# Revit family: OHMH-NRG
name_source: partatom
category: Mechanical Equipment
units: mm (PartAtom-declared; Revit-internal decimal feet)

## family parameters
Always vertical = Yes
Cut with Voids When Loaded = No
OmniClass Number = 23.40.40.11.17
OmniClass Title = Refrigerated Cases
Part Type = Normal
Room Calculation Point = No
Round Connector Dimension = Use Radius
Shared = No
Work Plane-Based = Yes

## types (12) — shared parameters
16" Shelf = Yes
18" Shelf = Yes
20" Shelf = Yes
BOTTOM ELECTRICAL = Yes
BOTTOM REFRIGERATION PIPING = Yes
Certifications = NSF 7, UL471, CSA
DATE = 05/16/2016
DESIGNERS NAME = SHIDDRAMESH
DRAIN PIPING = Yes
Default Elevation = 48"
Defrosts Per Day = 6
Description = High Multi-Deck Merchandiser
Discharge Air (°F) = 30 °F
Discharge Air Velocity (FPM) = 200 FPM
EQUIPMENT DESCRIPTION = High Multi-Deck Merchandiser
EQUIPMENT MARK = OHMH-NRG-5BF
Evaporator (°F) = 27 °F
GLASS = Glass
Height = 75"
High Efficiency Amps = 1 A
Item Description = High Multi-Deck Merchandiser
LF STD END = Yes
Legend Number = OHMH-NRG-5BF
Manufacturer = HILL PHOENIX
Model = OHMH-NRG-5BF
PAINTED METAL UPPER SHELF = PAINTED SHELVES
REAR REFRIGERATION PIPING = Yes
REFRIGERATION PIPING = COPPER PIPE
RT STD END = Yes
STAINLESS STEEL = GALVANIZED STEEL
Standard Power Amps = 0 A
Superheat Set Point @ Bulb (°F) = 6-8 °F
TOP ELECTRICAL = Yes
TOP REFRIGERATION PIPING = Yes
Timed-Off Defrost Fail-Safe (Min) = 40 (mIN)
Timed-Off Defrost Termination Temp = 42 °F
URL = http://www.hillphoenix.com
Width = 43 1/4"

## per-type parameters (varying)
| type | Application Discipline | BTUH Conventional | BTUH Parallel | CENTER LINE | DRAIN LINE | Front Sill Height | High Efficiency Watts | High Power (Cornice) Amps | High Power (Cornice) Watts | Length | Length of Cases | Light Length | Lights Per Row | Number of Fans | Refgn | Standard Power Watts |
| 04' Standard Front Sill Height | Standard Front Sill Height | 1531 | 1340 | 24" | 36" |  | 36 W | 0 A | 22 W | 48" | 48" | 4' | 1 | 2 | 22 1/2" | 12 W |
| 06' Standard Front Sill Height | Standard Front Sill Height | 1531 | 1340 | 36" | 36" |  | 54 W | 0 A | 30 W | 72" | 72" | 3' | 200000 | 3 | 28 5/8" | 17 W |
| 08' Standard Front Sill Height | Standard Front Sill Height | 1531 | 1340 | 48" | 48" |  | 54 W | 0 A | 43 W | 96" | 96" | 4' | 2 | 3 | 28 5/8" | 24 W |
| 12' Standard Front Sill Height | Standard Front Sill Height | 1531 | 1340 | 72" | 72" |  | 72 W | 1 A | 65 W | 144" | 144" | 4' | 3 | 4 | 28 5/8" | 36 W |
| 04' All Other Front Sill Height | All Other Front Sill Height | 1410 | 1234 | 24" | 36" |  | 36 W | 0 A | 22 W | 48" | 48" | 4' | 1 | 2 | 22 1/2" | 12 W |
| 06' All Other Front Sill Height | All Other Front Sill Height | 1410 | 1234 | 36" | 36" |  | 54 W | 0 A | 30 W | 72" | 72" | 3' | 200000 | 3 | 28 5/8" | 17 W |
| 08' All Other Front Sill Height | All Other Front Sill Height | 1410 | 1234 | 48" | 48" |  | 54 W | 0 A | 43 W | 96" | 96" | 4' | 2 | 3 | 28 5/8" | 24 W |
| 12' All Other Front Sill Height | All Other Front Sill Height | 1410 | 1234 | 72" | 72" |  | 72 W | 1 A | 65 W | 144" | 144" | 4' | 3 | 4 | 28 5/8" | 36 W |
| 12' | All Other Front Sill Height | 1410 | 1234 | 72" | 72" | All others | 72 W | 0 A | 45 W | 144" | 48" | 4' | 3 | 4 | 28 5/8" | 18 W |
| 8' | All Other Front Sill Height | 1410 | 1234 | 48" | 48" | All others | 54 W | 0 A | 30 W | 96" | 48" | 4' | 2 | 3 | 28 5/8" | 12 W |
| 6' | All Other Front Sill Height | 1410 | 1234 | 36" | 36" | All others | 54 W | 0 A | 24 W | 72" | 48" | 3' | 2 | 3 | 28 5/8" | 9 W |
| 4' | All Other Front Sill Height | 1531 | 1340 | 24" | 36" | Standard | 36 W | 0 A | 15 W | 48" | 48" | 4' | 1 | 2 | 22 1/2" | 6 W |

## geometry (parser evidence)
native form markers: Blend x34, Sweep x14
no freeform markers — native parametric forms only
